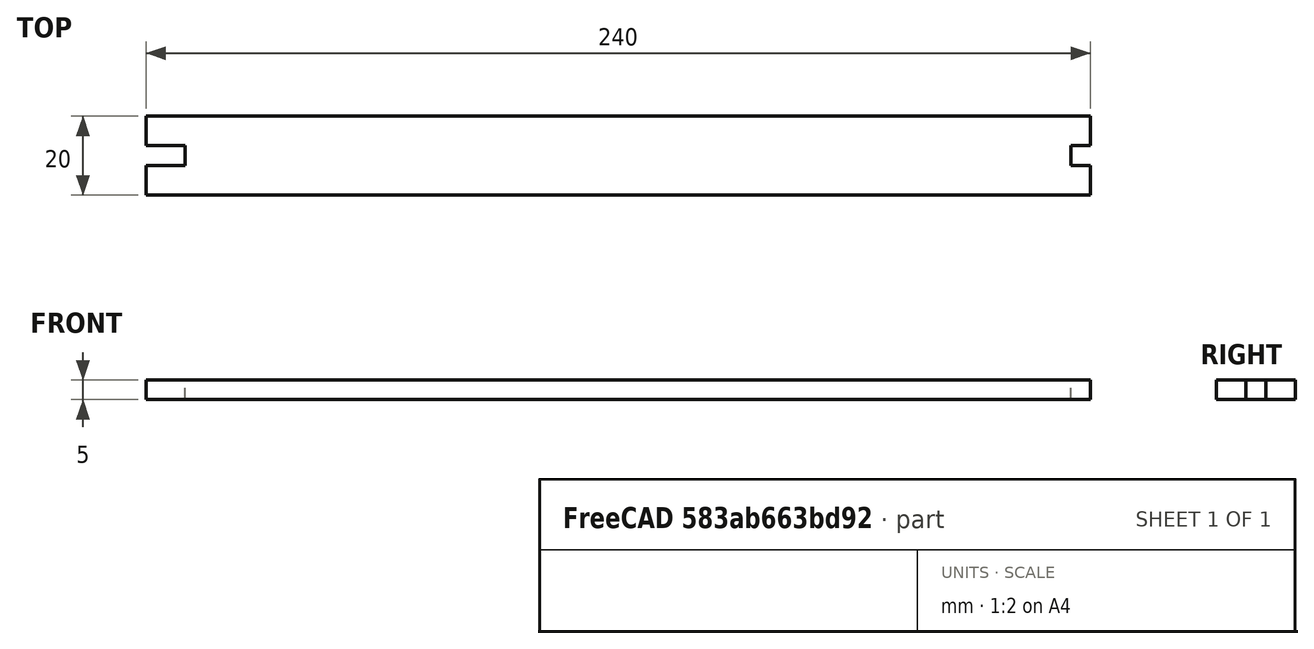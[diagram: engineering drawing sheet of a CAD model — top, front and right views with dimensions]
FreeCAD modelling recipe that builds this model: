
FCSTD DOCUMENT  (FreeCAD 1.0R39319 (Git))
Label: X Axis Near Leg
License: All rights reserved
LicenseURL: https://en.wikipedia.org/wiki/All_rights_reserved
objects: PartDesign::CoordinateSystem×2, Sketcher::SketchObject×1, PartDesign::Pad×1, PartDesign::Body×1, App::Part×1
note: 8 computed .brp shape members not serialized (recipe doc carries the construction recipe); baked Part::Feature solids carry a one-line shape summary decoded from their .brp

FEATURE [Sketcher::SketchObject] Sketch
  ArcFitTolerance = 1e-06
  AttachmentSupport = -> [XY_Plane001]
  FullyConstrained = true
  MakeInternals = false
  MapMode = 5
  sketch-geometry (14):
    g0: LineSegment StartX=0 StartY=2.55 StartZ=0 EndX=0 EndY=10 EndZ=0
    g1: LineSegment StartX=0 StartY=10 StartZ=0 EndX=240 EndY=10 EndZ=0
    g2: LineSegment StartX=240 StartY=10 StartZ=0 EndX=240 EndY=2.55 EndZ=0
    g3: LineSegment StartX=240 StartY=2.55 StartZ=0 EndX=235 EndY=2.55 EndZ=0
    g4: LineSegment StartX=235 StartY=2.55 StartZ=0 EndX=235 EndY=-2.55 EndZ=0
    g5: LineSegment StartX=235 StartY=-2.55 StartZ=0 EndX=240 EndY=-2.55 EndZ=0
    g6: LineSegment StartX=240 StartY=-2.55 StartZ=0 EndX=240 EndY=-10 EndZ=0
    g7: LineSegment StartX=240 StartY=-10 StartZ=0 EndX=0 EndY=-10 EndZ=0
    g8: LineSegment StartX=0 StartY=-10 StartZ=0 EndX=0 EndY=-2.55 EndZ=0
    g9: LineSegment StartX=0 StartY=-2.55 StartZ=0 EndX=10 EndY=-2.55 EndZ=0
    g10: LineSegment StartX=10 StartY=-2.55 StartZ=0 EndX=10 EndY=2.55 EndZ=0
    g11: LineSegment StartX=10 StartY=2.55 StartZ=0 EndX=0 EndY=2.55 EndZ=0
    g12: GeomPoint [constr] X=10 Y=0 Z=0
    g13: GeomPoint [constr] X=235 Y=5e-16 Z=0
  constraints (38):
    c: Coincident(g0,g1)
    c: Horizontal(g1)
    c: Coincident(g1,g2)
    c: Coincident(g2,g3)
    c: Horizontal(g3)
    c: Coincident(g3,g4)
    c: Vertical(g4)
    c: Coincident(g4,g5)
    c: Horizontal(g5)
    c: Coincident(g5,g6)
    c: Coincident(g6,g7)
    c: Horizontal(g7)
    c: Coincident(g7,g8)
    c: Coincident(g8,g9)
    c: Coincident(g9,g10)
    c: Coincident(g10,g11)
    c: Coincident(g11,g0)
    c: Vertical(g0)
    c: Horizontal(g11)
    c: Horizontal(g9)
    c: Vertical(g10)
    c: Vertical(g8)
    c: Vertical(g2)
    c: Vertical(g6)
    c: PointOnObject(g0,g8)
    c: PointOnObject(g5,g2)
    c: Symmetric(g10,g10,g12)
    c: Symmetric(g4,g4,g13)
    c: Distance(g9,g11) = 5.1
    c: DistanceY(g4,g4) = 5.1
    c: Distance(g7,g1) = 20
    c: Distance(g12,g1) = 10
    c: Distance(g13,g1) = 10
    c: DistanceX(g3,g3) = 5
    c: DistanceX(g11,g11) = 10
    c: PointOnObject(g12,g-1)
    c: PointOnObject(g8,g-2)
    c: DistanceX(g1,g1) = 240
FEATURE [PartDesign::Pad] Pad
  Direction = (0,0,1)
  Length = 5
  Length2 = 10
  Midplane = true
  Profile = -> Sketch
  ReferenceAxis = -> Sketch [N_Axis]
  Refine = true
  Suppressed = false
  Type = 0
FEATURE [PartDesign::Body] Body  label="X Axis Near Leg001"
  AllowCompound = false
  Group = -> [Sketch,Pad]
  Origin = -> Origin001
  Tip = -> Pad
FEATURE [PartDesign::CoordinateSystem] LCS_1
  AttacherType = Attacher::AttachEngine3D
  AttachmentOffset = pos=(10,0,0) rot=(0,0,1;0rad)
  AttachmentSupport = -> [XY_Plane001]
  MapMode = 2
  Placement = pos=(10,0,0) rot=(0,0,1;0rad)
FEATURE [PartDesign::CoordinateSystem] LCS_2
  AttacherType = Attacher::AttachEngine3D
  AttachmentOffset = pos=(235,0,0) rot=(0,0,1;0rad)
  AttachmentSupport = -> [XY_Plane001]
  MapMode = 2
  Placement = pos=(235,0,0) rot=(0,0,1;0rad)
FEATURE [App::Part] Part  label="X Axis Near Leg"
  Group = -> [Body,LCS_1,LCS_2]
  Origin = -> Origin
